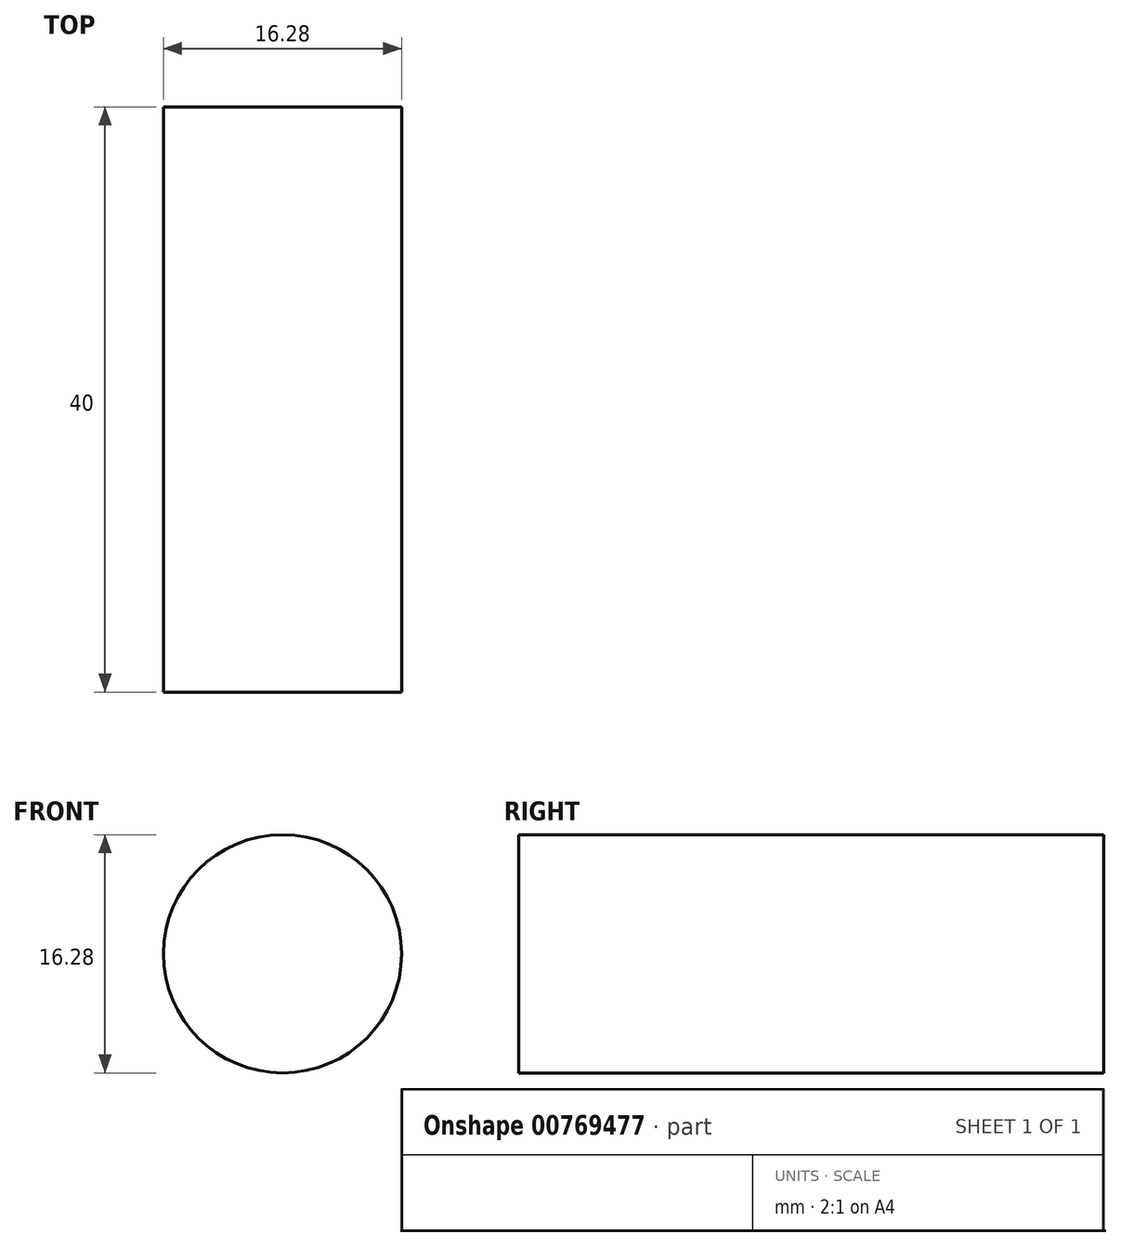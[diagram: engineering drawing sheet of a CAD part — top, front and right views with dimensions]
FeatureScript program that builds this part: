
annotation { "Feature Type Name" : "Feature", "Feature Type Description" : "" }
export const myFeature = defineFeature(function(context is Context, id is Id, definition is map)
    precondition{}
    {
        {
            var Q0;
            Q0=qCreatedBy(makeId("Front.planeOp"),FACE);
            var sketch = newSketch(context, id + "F0", { "sketchPlane" : qUnion([Q0])});
            skCircle(sketch, "E0", {"center": v(0, 0) * mm, "radius": 8.14 * mm});
            skSolve(sketch);
        }
        {
            var Q0;
            Q0=makeQuery(id+"F0.imprint","IMPRINT",FACE,{"disambiguationData":[TD([[makeQuery(id+"F0.imprint","IMPRINT",EDGE,{"derivedFrom":sQuery(id+"F0.wireOp",EDGE,"E0")}),1.0]])]});
            extrude(context, id + "F1", {"entities" : qUnion([Q0]), "depth" : 40 * mm, "offsetDistance" : 25 * mm});
        }
    });
